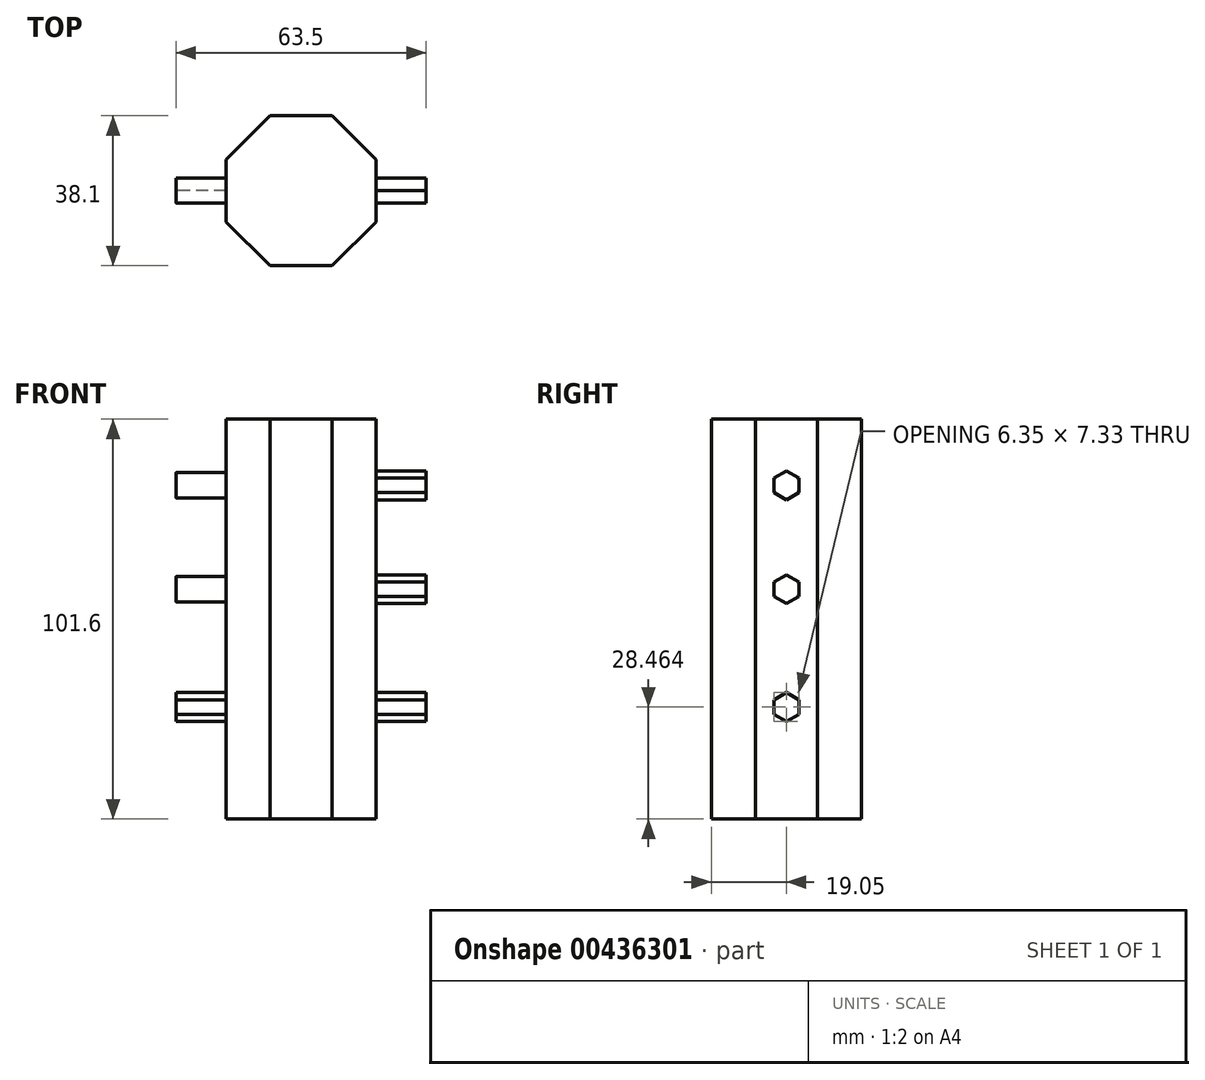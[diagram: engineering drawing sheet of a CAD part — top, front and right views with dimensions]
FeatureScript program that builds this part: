
annotation { "Feature Type Name" : "Feature", "Feature Type Description" : "" }
export const myFeature = defineFeature(function(context is Context, id is Id, definition is map)
    precondition{}
    {
        {
            var Q0;
            Q0=qCreatedBy(makeId("Top.planeOp"),FACE);
            var sketch = newSketch(context, id + "F0", { "sketchPlane" : qUnion([Q0])});
            skCircle(sketch, "E0.cCircle", {"center": v(0, 0) * mm, "radius": 19.05 * mm, "construction": true});
            skLineSegment(sketch, "E0.0", {"start": v(19.05, 7.9) * mm, "end": v(19.05, -7.9) * mm});
            skLineSegment(sketch, "E0.1", {"start": v(19.05, -7.9) * mm, "end": v(7.9, -19.05) * mm});
            skLineSegment(sketch, "E0.2", {"start": v(7.9, -19.05) * mm, "end": v(-7.9, -19.05) * mm});
            skLineSegment(sketch, "E0.3", {"start": v(-7.9, -19.05) * mm, "end": v(-19.05, -7.9) * mm});
            skLineSegment(sketch, "E0.4", {"start": v(-19.05, -7.9) * mm, "end": v(-19.05, 7.9) * mm});
            skLineSegment(sketch, "E0.5", {"start": v(-19.05, 7.9) * mm, "end": v(-7.9, 19.05) * mm});
            skLineSegment(sketch, "E0.6", {"start": v(-7.9, 19.05) * mm, "end": v(7.9, 19.05) * mm});
            skLineSegment(sketch, "E0.7", {"start": v(7.9, 19.05) * mm, "end": v(19.05, 7.9) * mm});
            skPoint(sketch, "E0.0.midPoint", {"position": v(19.05, 0) * mm});
            skSolve(sketch);
        }
        {
            var Q0;
            Q0 = qSketchRegion(id + "F0", true);
            extrude(context, id + "F1", {"entities" : qUnion([Q0]), "depth" : 101.6 * mm});
        }
        {
            var Q0;
            Q0=makeQuery(id+"F1.opExtrude","SWEPT_FACE",FACE,{"disambiguationData":[OSD([sQuery(id+"F0.wireOp",EDGE,"E0.0")])]});
            var sketch = newSketch(context, id + "F2", { "sketchPlane" : qUnion([Q0])});
            skCircle(sketch, "E1.cCircle", {"center": v(0, 84.8) * mm, "radius": 3.18 * mm, "construction": true});
            skLineSegment(sketch, "E1.0", {"start": v(3.18, 86.64) * mm, "end": v(3.18, 82.98) * mm});
            skLineSegment(sketch, "E1.1", {"start": v(3.17, 82.98) * mm, "end": v(0, 81.14) * mm});
            skLineSegment(sketch, "E1.2", {"start": v(0, 81.14) * mm, "end": v(-3.18, 82.98) * mm});
            skLineSegment(sketch, "E1.3", {"start": v(-3.18, 82.98) * mm, "end": v(-3.18, 86.64) * mm});
            skLineSegment(sketch, "E1.4", {"start": v(-3.17, 86.64) * mm, "end": v(0, 88.48) * mm});
            skLineSegment(sketch, "E1.5", {"start": v(0, 88.48) * mm, "end": v(3.17, 86.64) * mm});
            skPoint(sketch, "E1.0.midPoint", {"position": v(3.17, 84.8) * mm});
            skCircle(sketch, "E2.cCircle", {"center": v(0, 58.43) * mm, "radius": 3.18 * mm, "construction": true});
            skLineSegment(sketch, "E2.0", {"start": v(3.18, 60.26) * mm, "end": v(3.18, 56.6) * mm});
            skLineSegment(sketch, "E2.1", {"start": v(3.18, 56.6) * mm, "end": v(0, 54.76) * mm});
            skLineSegment(sketch, "E2.2", {"start": v(0, 54.76) * mm, "end": v(-3.18, 56.6) * mm});
            skLineSegment(sketch, "E2.3", {"start": v(-3.18, 56.6) * mm, "end": v(-3.18, 60.26) * mm});
            skLineSegment(sketch, "E2.4", {"start": v(-3.18, 60.26) * mm, "end": v(0, 62.1) * mm});
            skLineSegment(sketch, "E2.5", {"start": v(0, 62.1) * mm, "end": v(3.18, 60.26) * mm});
            skPoint(sketch, "E2.0.midPoint", {"position": v(3.18, 58.43) * mm});
            skCircle(sketch, "E3.cCircle", {"center": v(0, 28.46) * mm, "radius": 3.18 * mm, "construction": true});
            skLineSegment(sketch, "E3.0", {"start": v(3.18, 30.3) * mm, "end": v(3.18, 26.63) * mm});
            skLineSegment(sketch, "E3.1", {"start": v(3.18, 26.63) * mm, "end": v(0, 24.8) * mm});
            skLineSegment(sketch, "E3.2", {"start": v(0, 24.8) * mm, "end": v(-3.18, 26.63) * mm});
            skLineSegment(sketch, "E3.3", {"start": v(-3.17, 26.63) * mm, "end": v(-3.18, 30.3) * mm});
            skLineSegment(sketch, "E3.4", {"start": v(-3.17, 30.3) * mm, "end": v(0, 32.13) * mm});
            skLineSegment(sketch, "E3.5", {"start": v(0, 32.13) * mm, "end": v(3.18, 30.3) * mm});
            skPoint(sketch, "E3.0.midPoint", {"position": v(3.18, 28.46) * mm});
            skSolve(sketch);
        }
        {
            var Q0;
            Q0=makeQuery(id+"F2.imprint","IMPRINT",FACE,{"disambiguationData":[TD([[makeQuery(id+"F2.imprint","IMPRINT",EDGE,{"derivedFrom":sQuery(id+"F2.wireOp",EDGE,"E1.0")}),-1.0]])]});
            var Q1;
            Q1=makeQuery(id+"F2.imprint","IMPRINT",FACE,{"disambiguationData":[TD([[makeQuery(id+"F2.imprint","IMPRINT",EDGE,{"derivedFrom":sQuery(id+"F2.wireOp",EDGE,"E2.0")}),-1.0]])]});
            var Q2;
            Q2=makeQuery(id+"F2.imprint","IMPRINT",FACE,{"disambiguationData":[TD([[makeQuery(id+"F2.imprint","IMPRINT",EDGE,{"derivedFrom":sQuery(id+"F2.wireOp",EDGE,"E3.0")}),-1.0]])]});
            extrude(context, id + "F3", {"entities" : qUnion([Q0, Q1, Q2]), "operationType" : NewBodyOperationType.ADD, "depth" : 12.7 * mm, "hasSecondDirection" : true, "secondDirectionOppositeDirection" : true, "secondDirectionDepth" : 50.8 * mm});
        }
        {
            var Q0;
            {var subQ0=sQuery(id+"F2.wireOp",EDGE,"E1.0");var subQ1=sQuery(id+"F2.wireOp",EDGE,"E1.5");Q0=makeQuery(id+"F3.boolean.opBoolean","SPLIT",EDGE,{"disambiguationData":[TD([makeQuery(id+"F1.opExtrude","SWEPT_FACE",FACE,{"disambiguationData":[OSD([sQuery(id+"F0.wireOp",EDGE,"E0.4")])]})])],"derivedFrom":makeQuery(id+"F3.opExtrude","SWEPT_EDGE",EDGE,{"disambiguationData":[OSD([subQ0,subQ1])]})});}
            var Q1;
            {var subQ0=sQuery(id+"F2.wireOp",EDGE,"E1.1");var subQ1=sQuery(id+"F2.wireOp",EDGE,"E1.0");Q1=makeQuery(id+"F3.boolean.opBoolean","SPLIT",EDGE,{"disambiguationData":[TD([makeQuery(id+"F1.opExtrude","SWEPT_FACE",FACE,{"disambiguationData":[OSD([sQuery(id+"F0.wireOp",EDGE,"E0.4")])]})])],"derivedFrom":makeQuery(id+"F3.opExtrude","SWEPT_EDGE",EDGE,{"disambiguationData":[OSD([subQ1,subQ0])]})});}
            var Q2;
            {var subQ0=sQuery(id+"F2.wireOp",EDGE,"E1.1");var subQ1=sQuery(id+"F2.wireOp",EDGE,"E1.2");Q2=makeQuery(id+"F3.boolean.opBoolean","SPLIT",EDGE,{"disambiguationData":[TD([makeQuery(id+"F1.opExtrude","SWEPT_FACE",FACE,{"disambiguationData":[OSD([sQuery(id+"F0.wireOp",EDGE,"E0.4")])]})])],"derivedFrom":makeQuery(id+"F3.opExtrude","SWEPT_EDGE",EDGE,{"disambiguationData":[OSD([subQ0,subQ1])]})});}
            var Q3;
            {var subQ0=sQuery(id+"F2.wireOp",EDGE,"E1.3");var subQ1=sQuery(id+"F2.wireOp",EDGE,"E1.2");Q3=makeQuery(id+"F3.boolean.opBoolean","SPLIT",EDGE,{"disambiguationData":[TD([makeQuery(id+"F1.opExtrude","SWEPT_FACE",FACE,{"disambiguationData":[OSD([sQuery(id+"F0.wireOp",EDGE,"E0.4")])]})])],"derivedFrom":makeQuery(id+"F3.opExtrude","SWEPT_EDGE",EDGE,{"disambiguationData":[OSD([subQ1,subQ0])]})});}
            var Q4;
            {var subQ0=sQuery(id+"F2.wireOp",EDGE,"E1.4");var subQ1=sQuery(id+"F2.wireOp",EDGE,"E1.3");Q4=makeQuery(id+"F3.boolean.opBoolean","SPLIT",EDGE,{"disambiguationData":[TD([makeQuery(id+"F1.opExtrude","SWEPT_FACE",FACE,{"disambiguationData":[OSD([sQuery(id+"F0.wireOp",EDGE,"E0.4")])]})])],"derivedFrom":makeQuery(id+"F3.opExtrude","SWEPT_EDGE",EDGE,{"disambiguationData":[OSD([subQ1,subQ0])]})});}
            var Q5;
            {var subQ0=sQuery(id+"F2.wireOp",EDGE,"E1.5");var subQ1=sQuery(id+"F2.wireOp",EDGE,"E1.4");Q5=makeQuery(id+"F3.boolean.opBoolean","SPLIT",EDGE,{"disambiguationData":[TD([makeQuery(id+"F1.opExtrude","SWEPT_FACE",FACE,{"disambiguationData":[OSD([sQuery(id+"F0.wireOp",EDGE,"E0.4")])]})])],"derivedFrom":makeQuery(id+"F3.opExtrude","SWEPT_EDGE",EDGE,{"disambiguationData":[OSD([subQ1,subQ0])]})});}
            fillet(context, id + "F4", {"entities" : qUnion([Q0, Q1, Q2, Q3, Q4, Q5]), "radius" : 2.54 * mm, "tangentPropagation" : true, "allowEdgeOverflow" : false});
        }
        {
            var Q0;
            {var subQ0=sQuery(id+"F2.wireOp",EDGE,"E2.5");var subQ1=sQuery(id+"F2.wireOp",EDGE,"E2.4");Q0=makeQuery(id+"F3.boolean.opBoolean","SPLIT",EDGE,{"disambiguationData":[TD([makeQuery(id+"F1.opExtrude","SWEPT_FACE",FACE,{"disambiguationData":[OSD([sQuery(id+"F0.wireOp",EDGE,"E0.4")])]})])],"derivedFrom":makeQuery(id+"F3.opExtrude","SWEPT_EDGE",EDGE,{"disambiguationData":[OSD([subQ1,subQ0])]})});}
            var Q1;
            {var subQ0=sQuery(id+"F2.wireOp",EDGE,"E2.3");var subQ1=sQuery(id+"F2.wireOp",EDGE,"E2.2");Q1=makeQuery(id+"F3.boolean.opBoolean","SPLIT",EDGE,{"disambiguationData":[TD([makeQuery(id+"F1.opExtrude","SWEPT_FACE",FACE,{"disambiguationData":[OSD([sQuery(id+"F0.wireOp",EDGE,"E0.4")])]})])],"derivedFrom":makeQuery(id+"F3.opExtrude","SWEPT_EDGE",EDGE,{"disambiguationData":[OSD([subQ1,subQ0])]})});}
            var Q2;
            {var subQ0=sQuery(id+"F2.wireOp",EDGE,"E2.2");var subQ1=sQuery(id+"F2.wireOp",EDGE,"E2.1");Q2=makeQuery(id+"F3.boolean.opBoolean","SPLIT",EDGE,{"disambiguationData":[TD([makeQuery(id+"F1.opExtrude","SWEPT_FACE",FACE,{"disambiguationData":[OSD([sQuery(id+"F0.wireOp",EDGE,"E0.4")])]})])],"derivedFrom":makeQuery(id+"F3.opExtrude","SWEPT_EDGE",EDGE,{"disambiguationData":[OSD([subQ1,subQ0])]})});}
            var Q3;
            {var subQ0=sQuery(id+"F2.wireOp",EDGE,"E2.0");var subQ1=sQuery(id+"F2.wireOp",EDGE,"E2.1");Q3=makeQuery(id+"F3.boolean.opBoolean","SPLIT",EDGE,{"disambiguationData":[TD([makeQuery(id+"F1.opExtrude","SWEPT_FACE",FACE,{"disambiguationData":[OSD([sQuery(id+"F0.wireOp",EDGE,"E0.4")])]})])],"derivedFrom":makeQuery(id+"F3.opExtrude","SWEPT_EDGE",EDGE,{"disambiguationData":[OSD([subQ0,subQ1])]})});}
            var Q4;
            {var subQ0=sQuery(id+"F2.wireOp",EDGE,"E2.0");var subQ1=sQuery(id+"F2.wireOp",EDGE,"E2.5");Q4=makeQuery(id+"F3.boolean.opBoolean","SPLIT",EDGE,{"disambiguationData":[TD([makeQuery(id+"F1.opExtrude","SWEPT_FACE",FACE,{"disambiguationData":[OSD([sQuery(id+"F0.wireOp",EDGE,"E0.4")])]})])],"derivedFrom":makeQuery(id+"F3.opExtrude","SWEPT_EDGE",EDGE,{"disambiguationData":[OSD([subQ0,subQ1])]})});}
            var Q5;
            {var subQ0=sQuery(id+"F2.wireOp",EDGE,"E2.3");var subQ1=sQuery(id+"F2.wireOp",EDGE,"E2.4");Q5=makeQuery(id+"F3.boolean.opBoolean","SPLIT",EDGE,{"disambiguationData":[TD([makeQuery(id+"F1.opExtrude","SWEPT_FACE",FACE,{"disambiguationData":[OSD([sQuery(id+"F0.wireOp",EDGE,"E0.4")])]})])],"derivedFrom":makeQuery(id+"F3.opExtrude","SWEPT_EDGE",EDGE,{"disambiguationData":[OSD([subQ0,subQ1])]})});}
            fillet(context, id + "F5", {"entities" : qUnion([Q0, Q1, Q2, Q3, Q4, Q5]), "radius" : 2.54 * mm, "tangentPropagation" : true, "allowEdgeOverflow" : false});
        }
    });
